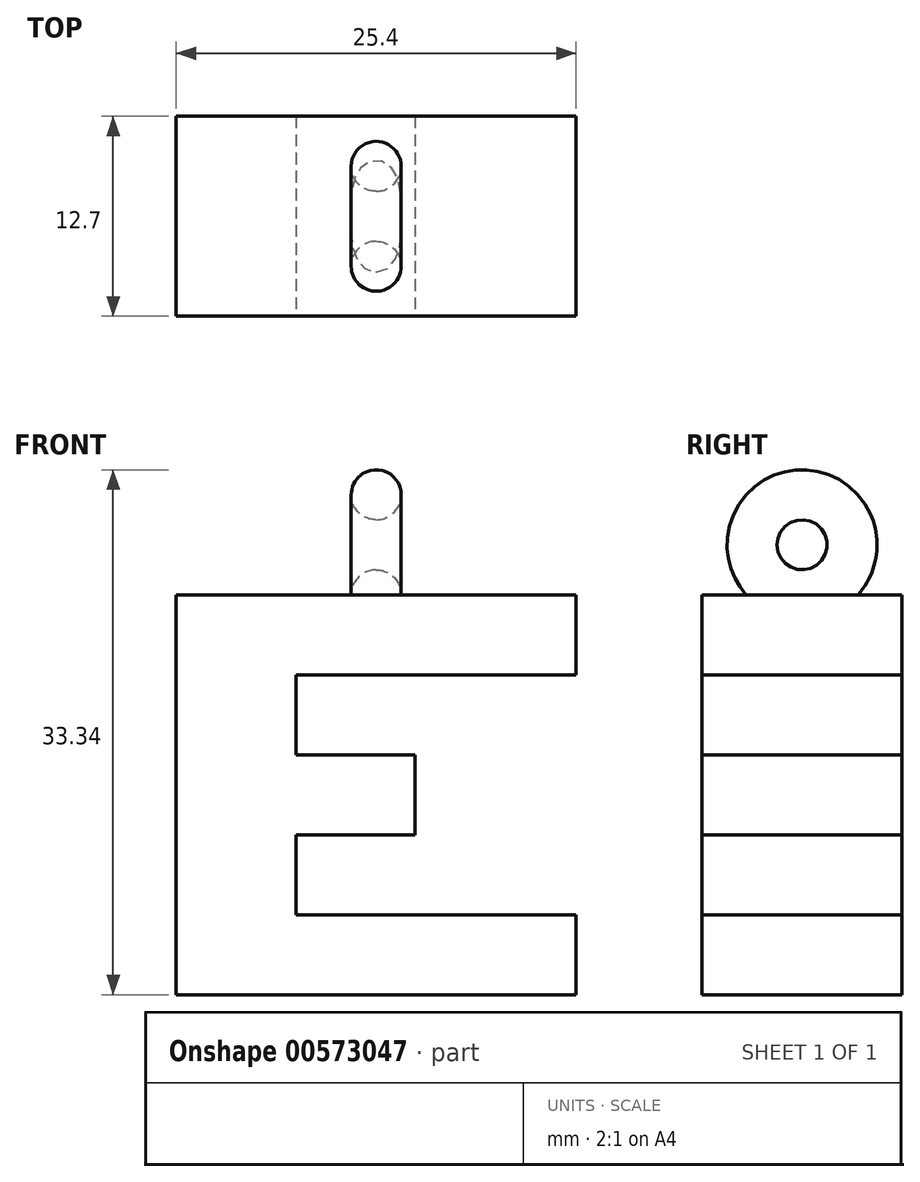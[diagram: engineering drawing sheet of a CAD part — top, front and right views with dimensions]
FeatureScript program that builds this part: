
annotation { "Feature Type Name" : "Feature", "Feature Type Description" : "" }
export const myFeature = defineFeature(function(context is Context, id is Id, definition is map)
    precondition{}
    {
        {
            var Q0;
            Q0=qCreatedBy(makeId("Front.planeOp"),FACE);
            var sketch = newSketch(context, id + "F0", { "sketchPlane" : qUnion([Q0])});
            skLineSegment(sketch, "E0", {"start": v(0, 0) * mm, "end": v(0, 25.4) * mm});
            skLineSegment(sketch, "E1", {"start": v(0, 25.4) * mm, "end": v(25.4, 25.4) * mm});
            skLineSegment(sketch, "E2", {"start": v(25.4, 25.4) * mm, "end": v(25.4, 0) * mm});
            skLineSegment(sketch, "E3", {"start": v(25.4, 0) * mm, "end": v(0, 0) * mm});
            skSolve(sketch);
        }
        {
            var Q0;
            Q0 = qSketchRegion(id + "F0", true);
            extrude(context, id + "F1", {"entities" : qUnion([Q0]), "depth" : 12.7 * mm, "offsetDistance" : 25.4 * mm});
        }
        {
            var Q0;
            Q0=makeQuery(id+"F1.opExtrude","CAP_FACE",FACE,{"disambiguationData":[OSD([sQuery(id+"F0.wireOp",EDGE,"E0"),sQuery(id+"F0.wireOp",EDGE,"E1"),sQuery(id+"F0.wireOp",EDGE,"E2"),sQuery(id+"F0.wireOp",EDGE,"E3")])],"isStart":false});
            var sketch = newSketch(context, id + "F2", { "sketchPlane" : qUnion([Q0])});
            skLineSegment(sketch, "E4", {"start": v(25.4, 25.4) * mm, "end": v(25.4, 0) * mm});
            skLineSegment(sketch, "E5", {"start": v(25.4, 0) * mm, "end": v(0, 0) * mm});
            skLineSegment(sketch, "E6", {"start": v(0, 0) * mm, "end": v(0, 25.4) * mm});
            skLineSegment(sketch, "E7", {"start": v(0, 25.4) * mm, "end": v(25.4, 25.4) * mm});
            skLineSegment(sketch, "E8", {"start": v(25.4, 20.32) * mm, "end": v(7.62, 20.32) * mm});
            skLineSegment(sketch, "E9", {"start": v(7.62, 20.32) * mm, "end": v(7.62, 15.24) * mm});
            skLineSegment(sketch, "E10", {"start": v(7.62, 15.24) * mm, "end": v(15.18, 15.24) * mm});
            skLineSegment(sketch, "E11", {"start": v(15.18, 15.24) * mm, "end": v(15.18, 10.16) * mm});
            skLineSegment(sketch, "E12", {"start": v(15.18, 10.16) * mm, "end": v(7.62, 10.16) * mm});
            skLineSegment(sketch, "E13", {"start": v(7.62, 10.16) * mm, "end": v(7.62, 5.08) * mm});
            skLineSegment(sketch, "E14", {"start": v(7.62, 5.08) * mm, "end": v(25.4, 5.08) * mm});
            skPoint(sketch, "E15.centerSnap0", {"position": v(12.7, 25.4) * mm});
            skSolve(sketch);
        }
        {
            var Q0;
            {var subQ0=sQuery(id+"F2.wireOp",EDGE,"E8");Q0=makeQuery(id+"F2.imprint","IMPRINT",FACE,{"disambiguationData":[TD([[makeQuery(id+"F2.imprint","IMPRINT",EDGE,{"derivedFrom":subQ0}),1.0]])]});}
            var Q1;
            Q1=makeQuery(id+"F2.imprint","IMPRINT",FACE,{"disambiguationData":[TD([[makeQuery(id+"F2.imprint","IMPRINT",EDGE,{"derivedFrom":sQuery(id+"F2.wireOp",EDGE,"E15")}),1.0]])]});
            extrude(context, id + "F3", {"entities" : qUnion([Q0, Q1]), "operationType" : NewBodyOperationType.REMOVE, "oppositeDirection" : true, "depth" : 25.4 * mm, "offsetDistance" : 25.4 * mm});
        }
        {
            var Q0;
            Q0=qCreatedBy(makeId("Front.planeOp"),FACE);
            cPlane(context, id + "F4", {"entities" : qUnion([Q0]), "cplaneType" : CPlaneType.OFFSET, "offset" : 6.35 * mm, "width" : 152.4 * mm, "height" : 152.4 * mm});
        }
        {
            var Q0;
            Q0=qCreatedBy(id+"F4.planeOp",FACE);
            var sketch = newSketch(context, id + "F5", { "sketchPlane" : qUnion([Q0])});
            skCircle(sketch, "E16", {"center": v(12.7, 25.4) * mm, "radius": 1.59 * mm});
            skLineSegment(sketch, "E17", {"start": v(0, 28.58) * mm, "end": v(29.91, 28.58) * mm});
            skSolve(sketch);
        }
        {
            var Q0;
            Q0 = qSketchRegion(id + "F5", true);
            var Q1;
            Q1=sQuery(id+"F5.wireOp",EDGE,"E17");
            revolve(context, id + "F6", {"operationType" : NewBodyOperationType.ADD, "entities" : qUnion([Q0]), "axis" : qUnion([Q1]), "revolveType" : RevolveType.FULL});
        }
    });
